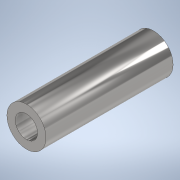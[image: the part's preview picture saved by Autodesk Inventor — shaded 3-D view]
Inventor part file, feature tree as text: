
AUTODESK INVENTOR PART (.ipt)
format: ipt  version: 2021 (Build 250183000, 183)  size: 105,472 bytes
history: native  units: mm
features: other x1, extrude x1, sketch x1
ambient origin geometry x8: Origin, YZ Plane, XZ Plane, XY Plane, X Axis, Y Axis, Z Axis, Center Point
bodies: Body1 (feature_tree)
feature tree (3):
  other  "Твердое тело1"
  extrude  "Выдавливание1"  Depth=28.0mm
  sketch  "Эскиз1"
